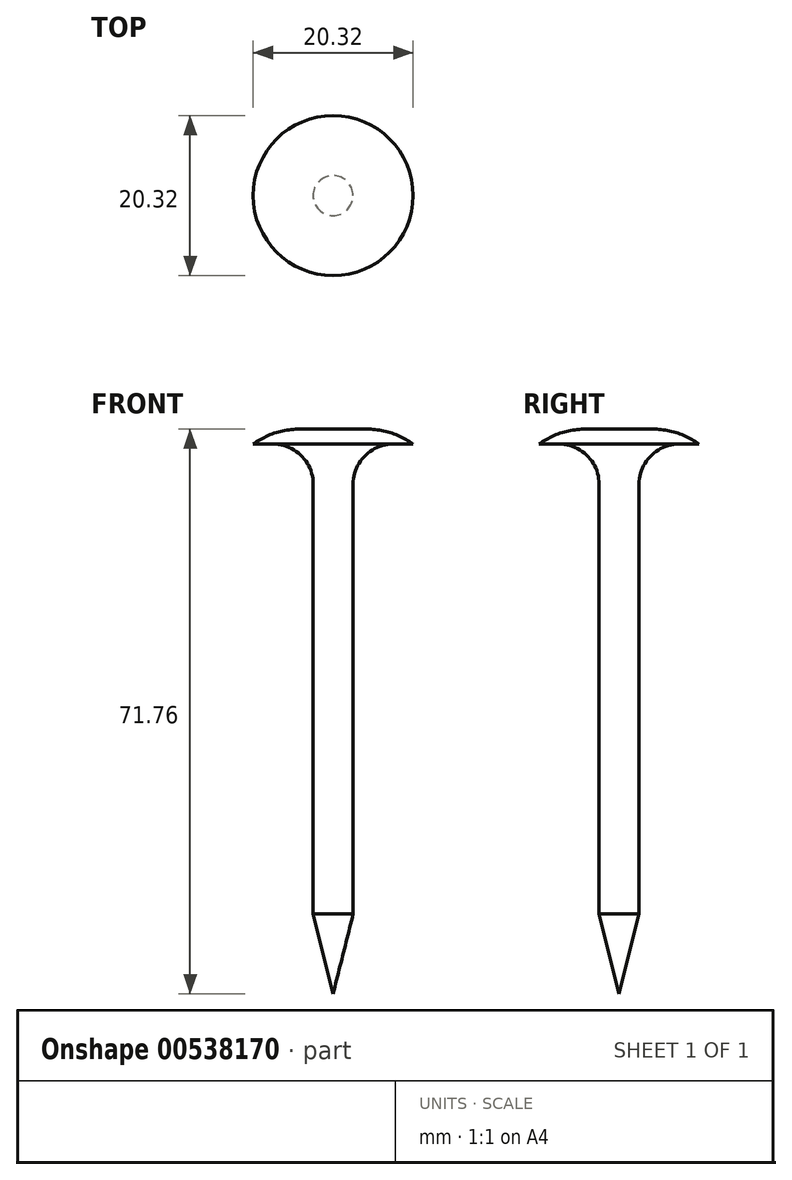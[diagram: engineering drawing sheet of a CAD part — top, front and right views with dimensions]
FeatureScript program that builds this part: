
annotation { "Feature Type Name" : "Feature", "Feature Type Description" : "" }
export const myFeature = defineFeature(function(context is Context, id is Id, definition is map)
    precondition{}
    {
        {
            var Q0;
            Q0=qCreatedBy(makeId("Front.planeOp"),FACE);
            var sketch = newSketch(context, id + "F0", { "sketchPlane" : qUnion([Q0])});
            skLineSegment(sketch, "E0.bottom", {"start": v(0, 12.7) * mm, "end": v(2.54, 12.7) * mm});
            skLineSegment(sketch, "E0.top", {"start": v(0, -57.15) * mm, "end": v(2.54, -57.15) * mm});
            skLineSegment(sketch, "E0.left", {"start": v(0, 12.7) * mm, "end": v(0, -57.15) * mm});
            skLineSegment(sketch, "E0.right", {"start": v(2.54, 12.7) * mm, "end": v(2.54, -57.15) * mm});
            skLineSegment(sketch, "E1.bottom", {"start": v(0, 14.6) * mm, "end": v(10.16, 14.6) * mm});
            skLineSegment(sketch, "E1.top", {"start": v(0, 12.7) * mm, "end": v(10.16, 12.7) * mm});
            skLineSegment(sketch, "E1.left", {"start": v(0, 14.6) * mm, "end": v(0, 12.7) * mm});
            skLineSegment(sketch, "E1.right", {"start": v(10.16, 14.6) * mm, "end": v(10.16, 12.7) * mm});
            skSolve(sketch);
        }
        {
            var Q0;
            Q0 = qSketchRegion(id + "F0", true);
            var Q1;
            Q1=sQuery(id+"F0.wireOp",EDGE,"E0.left");
            revolve(context, id + "F1", {"entities" : qUnion([Q0]), "axis" : qUnion([Q1]), "revolveType" : RevolveType.FULL});
        }
        {
            var Q0;
            Q0=makeQuery(id+"F1.opRevolve","SWEPT_EDGE",EDGE,{"disambiguationData":[OSD([sQuery(id+"F0.wireOp",EDGE,"E0.top"),sQuery(id+"F0.wireOp",EDGE,"E0.right")])]});
            chamfer(context, id + "F2", {"entities" : qUnion([Q0]), "chamferType" : ChamferType.TWO_OFFSETS, "width1" : 10.16 * mm, "oppositeDirection" : false, "width2" : 2.54 * mm, "tangentPropagation" : true});
        }
        {
            var Q0;
            Q0=makeQuery(id+"F1.opRevolve","SWEPT_EDGE",EDGE,{"disambiguationData":[OSD([sQuery(id+"F0.wireOp",EDGE,"E0.right"),sQuery(id+"F0.wireOp",EDGE,"E1.top")])]});
            fillet(context, id + "F3", {"entities" : qUnion([Q0]), "radius" : 5.08 * mm, "tangentPropagation" : true, "allowEdgeOverflow" : false});
        }
        {
            var Q0;
            Q0=makeQuery(id+"F1.opRevolve","SWEPT_EDGE",EDGE,{"disambiguationData":[OSD([sQuery(id+"F0.wireOp",EDGE,"E1.bottom"),sQuery(id+"F0.wireOp",EDGE,"E1.right")])]});
            fillet(context, id + "F4", {"entities" : qUnion([Q0]), "radius" : 10.16 * mm, "tangentPropagation" : true, "allowEdgeOverflow" : false});
        }
    });
